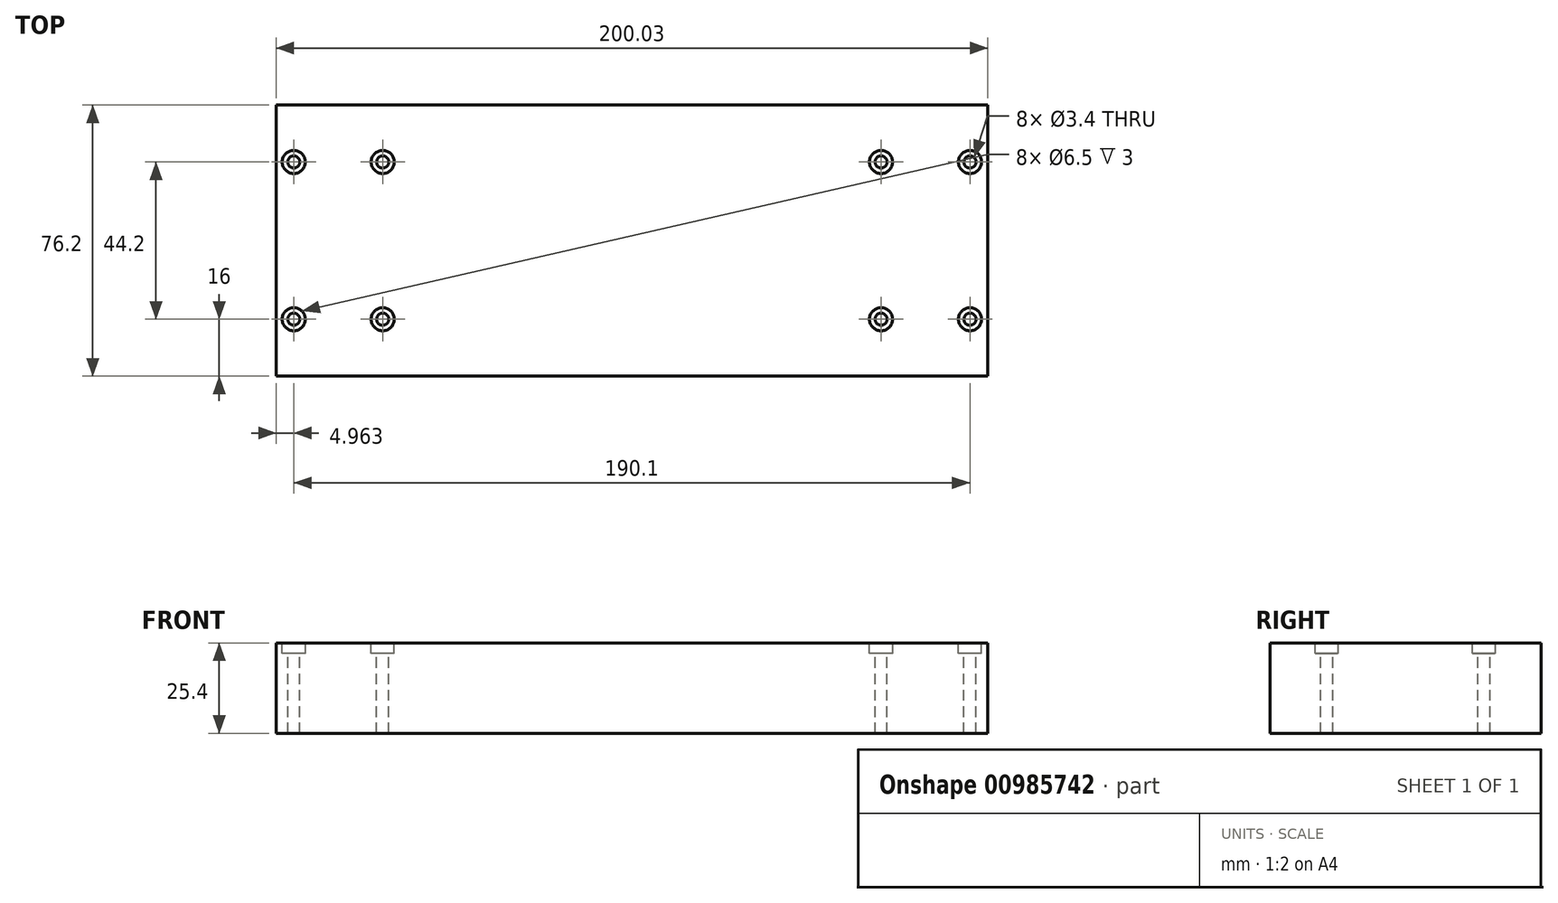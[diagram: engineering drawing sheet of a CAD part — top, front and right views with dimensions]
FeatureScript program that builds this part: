
annotation { "Feature Type Name" : "Feature", "Feature Type Description" : "" }
export const myFeature = defineFeature(function(context is Context, id is Id, definition is map)
    precondition{}
    {
        {
            var Q0;
            Q0=qCreatedBy(makeId("Top.planeOp"),FACE);
            var sketch = newSketch(context, id + "F0", { "sketchPlane" : qUnion([Q0])});
            skLineSegment(sketch, "E0.bottom", {"start": v(0, 0) * mm, "end": v(200.02, 0) * mm});
            skLineSegment(sketch, "E0.top", {"start": v(0, 76.2) * mm, "end": v(200.02, 76.2) * mm});
            skLineSegment(sketch, "E0.left", {"start": v(0, 0) * mm, "end": v(0, 76.2) * mm});
            skLineSegment(sketch, "E0.right", {"start": v(200.02, 0) * mm, "end": v(200.02, 76.2) * mm});
            skSolve(sketch);
        }
        {
            var Q0;
            Q0 = qSketchRegion(id + "F0", true);
            extrude(context, id + "F1", {"entities" : qUnion([Q0]), "depth" : 25.4 * mm, "offsetDistance" : 25.4 * mm});
        }
        {
            var Q0;
            Q0=makeQuery(id+"F1.opExtrude","CAP_FACE",FACE,{"disambiguationData":[OSD([sQuery(id+"F0.wireOp",EDGE,"E0.bottom"),sQuery(id+"F0.wireOp",EDGE,"E0.top"),sQuery(id+"F0.wireOp",EDGE,"E0.left"),sQuery(id+"F0.wireOp",EDGE,"E0.right")])],"isStart":false});
            var sketch = newSketch(context, id + "F2", { "sketchPlane" : qUnion([Q0])});
            skLineSegment(sketch, "E1", {"start": v(4.96, 60.2) * mm, "end": v(29.96, 60.2) * mm, "construction": true});
            skLineSegment(sketch, "E2", {"start": v(29.96, 60.2) * mm, "end": v(170.06, 60.2) * mm, "construction": true});
            skLineSegment(sketch, "E3", {"start": v(170.06, 60.2) * mm, "end": v(195.06, 60.2) * mm, "construction": true});
            skLineSegment(sketch, "E4", {"start": v(195.06, 60.2) * mm, "end": v(195.06, 16) * mm, "construction": true});
            skLineSegment(sketch, "E5", {"start": v(195.06, 16) * mm, "end": v(170.06, 16) * mm, "construction": true});
            skLineSegment(sketch, "E6", {"start": v(170.06, 16) * mm, "end": v(29.96, 16) * mm, "construction": true});
            skLineSegment(sketch, "E7", {"start": v(29.96, 16) * mm, "end": v(4.96, 16) * mm, "construction": true});
            skLineSegment(sketch, "E8", {"start": v(4.96, 16) * mm, "end": v(4.96, 60.2) * mm, "construction": true});
            skLineSegment(sketch, "E9", {"start": v(29.96, 60.2) * mm, "end": v(29.96, 16) * mm, "construction": true});
            skLineSegment(sketch, "E10", {"start": v(170.06, 60.2) * mm, "end": v(170.06, 16) * mm, "construction": true});
            skLineSegment(sketch, "E11", {"start": v(100.01, 60.2) * mm, "end": v(100.01, 76.2) * mm, "construction": true});
            skLineSegment(sketch, "E12", {"start": v(4.96, 38.1) * mm, "end": v(0, 38.1) * mm, "construction": true});
            skLineSegment(sketch, "E13", {"start": v(17.46, 60.2) * mm, "end": v(17.46, 16) * mm, "construction": true});
            skLineSegment(sketch, "E14", {"start": v(182.56, 60.2) * mm, "end": v(182.56, 16) * mm, "construction": true});
            skPoint(sketch, "E15", {"position": v(4.96, 60.2) * mm});
            skPoint(sketch, "E16", {"position": v(29.96, 60.2) * mm});
            skPoint(sketch, "E17", {"position": v(4.96, 16) * mm});
            skPoint(sketch, "E18", {"position": v(29.96, 16) * mm});
            skPoint(sketch, "E19", {"position": v(170.06, 60.2) * mm});
            skPoint(sketch, "E20", {"position": v(195.06, 60.2) * mm});
            skPoint(sketch, "E21", {"position": v(195.06, 16) * mm});
            skPoint(sketch, "E22", {"position": v(170.06, 16) * mm});
            skSolve(sketch);
        }
        {
            var Q0;
            Q0=sQuery(id+"F2.wireOp",VERTEX,"E15");
            var Q1;
            Q1=sQuery(id+"F2.wireOp",VERTEX,"E16");
            var Q2;
            Q2=sQuery(id+"F2.wireOp",VERTEX,"E17");
            var Q3;
            Q3=sQuery(id+"F2.wireOp",VERTEX,"E18");
            var Q4;
            Q4=sQuery(id+"F2.wireOp",VERTEX,"E19");
            var Q5;
            Q5=sQuery(id+"F2.wireOp",VERTEX,"E20");
            var Q6;
            Q6=sQuery(id+"F2.wireOp",VERTEX,"E22");
            var Q7;
            Q7=sQuery(id+"F2.wireOp",VERTEX,"E21");
            var Q8;
            Q8=makeQuery(id+"F1.opExtrude","SWEPT_BODY",BODY,{"disambiguationData":[OSD([sQuery(id+"F0.wireOp",EDGE,"E0.bottom"),sQuery(id+"F0.wireOp",EDGE,"E0.top"),sQuery(id+"F0.wireOp",EDGE,"E0.left"),sQuery(id+"F0.wireOp",EDGE,"E0.right")])]});
            hole(context, id + "F3", {"style" : HoleStyle.C_BORE, "endStyle" : HoleEndStyle.THROUGH, "standardTappedOrClearance" : lookupTablePath({ "fit" : "Normal", "standard" : "ISO", "size" : "M3", "type" : "Clearance" }), "standardBlindInLast" : lookupTablePath({ "fit" : "Normal", "standard" : "ISO", "engagement" : "75%", "pitch" : "0.5 mm", "size" : "M3", "type" : "Clearance & tapped" }), "holeDiameter" : 3.4 * mm, "cBoreDiameter" : 6.5 * mm, "cBoreDepth" : 3 * mm, "majorDiameter" : 3 * mm, "isTappedThrough" : true, "tappedDepth" : 19.05 * mm, "tapClearance" : 3, "startFromSketch" : true, "locations" : qUnion([Q0, Q1, Q2, Q3, Q4, Q5, Q6, Q7]), "scope" : qUnion([Q8])});
        }
    });
